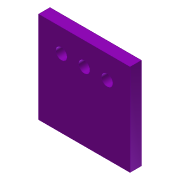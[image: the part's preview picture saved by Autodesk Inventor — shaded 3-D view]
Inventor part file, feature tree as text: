
AUTODESK INVENTOR PART (.ipt)
format: ipt  version: 2012 (Build 160160000, 160)  size: 84,480 bytes
history: native  units: in
note: dims shown in document units (in); Inventor stores cm internally (conversion verified against a paired STEP export)
features: extrude x2, sketch x2, pattern_linear x1
ambient origin geometry x8: Origin, YZ Plane, XZ Plane, XY Plane, X Axis, Y Axis, Z Axis, Center Point
bodies: Solid1 (feature_tree)
feature tree (5):
  extrude  "Extrusion1"  Depth=2.0in
  extrude  "Extrusion2"  Depth=0.5in
  pattern_linear  "Rectangular Pattern1"  Spacing1=0.5in  [1 undecoded]
  sketch  "Sketch1"  dims[d0=2.0in d1=2.0in]
  sketch  "Sketch2"  dims[d2=0.25in d3=0.0in d4=0.5in d5=0.5in d6=0.25in d7=0.25in d8=0.0in d9=1.1811in d11=0.5in]
note: 1 required parameter value undecoded (feature->parameter linkage not recoverable at this tier; creation-order binding heuristic only, values carry confidence <= 0.55)
